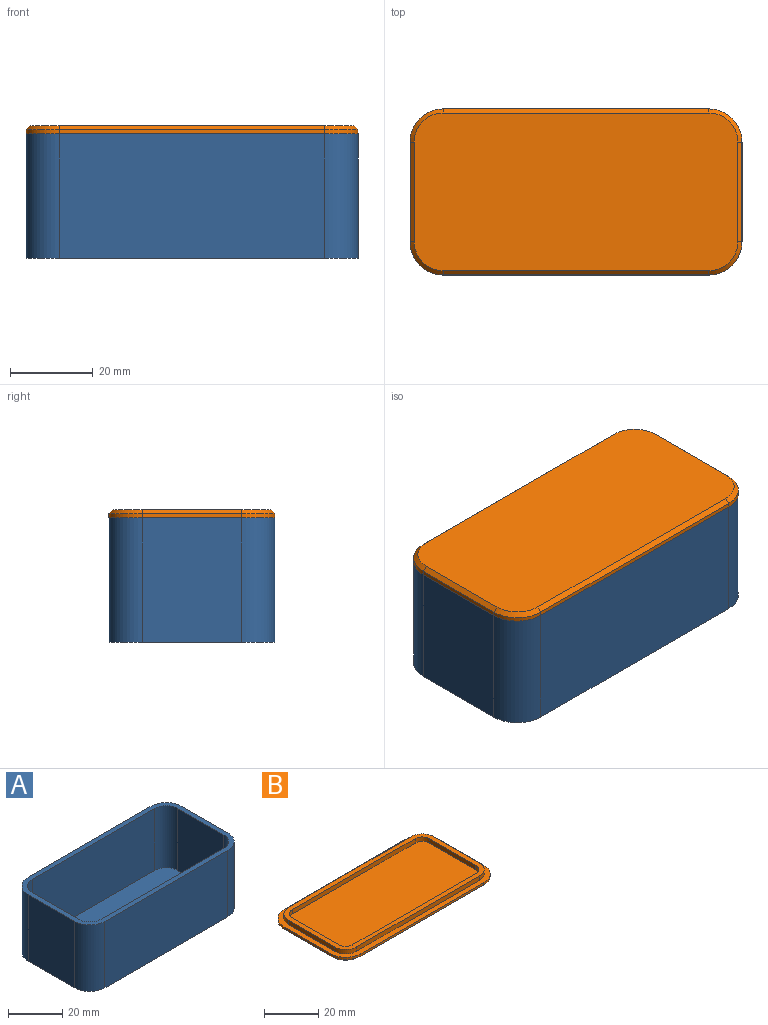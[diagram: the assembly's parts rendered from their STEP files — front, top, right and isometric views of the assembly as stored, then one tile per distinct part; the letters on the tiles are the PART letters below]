
ASSEMBLY  parts=2 mates=1
PART A: 19 faces, bbox 80x40x30 mm
  f0: plane 80x40mm, normal (0,0,1), area 440mm2, adj f1,f2,f3,f4,f5,f6,f7,f8
  f1: plane 30x24mm, normal (1,0,0), area 720mm2, adj f0,f2,f8,f9
  f2: cylinder r=8mm len=30mm, axis (0,0,-1), area 377mm2, adj f0,f1,f3,f9
  f3: plane 64x30mm, normal (0,1,0), area 1920mm2, adj f0,f2,f4,f9
  f4: cylinder r=8mm len=30mm, axis (0,0,-1), area 377mm2, adj f0,f3,f5,f9
  f5: plane 30x24mm, normal (-1,0,0), area 720mm2, adj f0,f4,f6,f9
  f6: cylinder r=8mm len=30mm, axis (0,0,-1), area 377mm2, adj f0,f5,f7,f9
  f7: plane 64x30mm, normal (0,-1,0), area 1920mm2, adj f0,f6,f8,f9
  f8: cylinder r=8mm len=30mm, axis (0,0,-1), area 377mm2, adj f0,f1,f7,f9
  f9: plane 80x40mm, normal (0,0,-1), area 3145.1mm2, adj f1,f2,f3,f4,f5,f6,f7,f8
  f10: plane 28x24mm, normal (-1,0,0), area 672mm2, adj f0,f11,f17,f18
  f11: cylinder r=6mm len=28mm, axis (0,0,-1), area 263.9mm2, adj f0,f10,f12,f18
  f12: plane 64x28mm, normal (0,-1,0), area 1792mm2, adj f0,f11,f13,f18
  f13: cylinder r=6mm len=28mm, axis (0,0,-1), area 263.9mm2, adj f0,f12,f14,f18
  f14: plane 28x24mm, normal (1,0,0), area 672mm2, adj f0,f13,f15,f18
  f15: cylinder r=6mm len=28mm, axis (0,0,-1), area 263.9mm2, adj f0,f14,f16,f18
  f16: plane 64x28mm, normal (0,1,0), area 1792mm2, adj f0,f15,f17,f18
  f17: cylinder r=6mm len=28mm, axis (0,0,-1), area 263.9mm2, adj f0,f10,f16,f18
  f18: plane 76x36mm, normal (0,0,1), area 2705.1mm2, adj f10,f11,f12,f13,f14,f15,f16,f17
PART B: 36 faces, bbox 80x40x4 mm
  f0: plane 24x1mm, normal (1,0,0), area 24mm2, adj f1,f7,f8,f33
  f1: cylinder r=8mm len=8mm, axis (0,0,-1), area 12.6mm2, adj f0,f2,f8,f35
  f2: plane 64x1mm, normal (0,1,0), area 64mm2, adj f1,f3,f8,f34
  f3: cylinder r=8mm len=8mm, axis (0,0,-1), area 12.6mm2, adj f2,f4,f8,f32
  f4: plane 24x1mm, normal (-1,0,0), area 24mm2, adj f3,f5,f8,f30
  f5: cylinder r=8mm len=8mm, axis (0,0,-1), area 12.6mm2, adj f4,f6,f8,f28
  f6: plane 64x1mm, normal (0,-1,0), area 64mm2, adj f5,f7,f8,f29
  f7: cylinder r=8mm len=8mm, axis (0,0,-1), area 12.6mm2, adj f0,f6,f8,f31
  f8: plane 80x40mm, normal (0,0,1), area 482.6mm2, adj f0,f1,f2,f3,f4,f5,f6,f7
  f9: plane 78x38mm, normal (0,0,-1), area 2921.9mm2, adj f28,f29,f30,f31,f32,f33,f34,f35
  f10: cylinder r=5.8mm len=5.8mm, axis (0,0,-1), area 18.2mm2, adj f8,f11,f25,f26
  f11: plane 64x2mm, normal (0,1,0), area 128mm2, adj f8,f10,f12,f26
  f12: cylinder r=5.8mm len=5.8mm, axis (0,0,-1), area 18.2mm2, adj f8,f11,f13,f26
  f13: plane 24x2mm, normal (-1,0,0), area 48mm2, adj f8,f12,f14,f26
  f14: cylinder r=5.8mm len=5.8mm, axis (0,0,-1), area 18.2mm2, adj f8,f13,f15,f26
  f15: plane 64x2mm, normal (0,-1,0), area 128mm2, adj f8,f14,f16,f26
  f16: cylinder r=5.8mm len=5.8mm, axis (0,0,-1), area 18.2mm2, adj f8,f15,f25,f26
  f17: cylinder r=3.8mm len=3.8mm, axis (0,0,-1), area 11.9mm2, adj f18,f24,f26,f27
  f18: plane 24x2mm, normal (-1,0,0), area 48mm2, adj f17,f19,f26,f27
  f19: cylinder r=3.8mm len=3.8mm, axis (0,0,-1), area 11.9mm2, adj f18,f20,f26,f27
  f20: plane 64x2mm, normal (0,1,0), area 128mm2, adj f19,f21,f26,f27
  f21: cylinder r=3.8mm len=3.8mm, axis (0,0,-1), area 11.9mm2, adj f20,f22,f26,f27
  f22: plane 24x2mm, normal (1,0,0), area 48mm2, adj f21,f23,f26,f27
  f23: cylinder r=3.8mm len=3.8mm, axis (0,0,-1), area 11.9mm2, adj f22,f24,f26,f27
  f24: plane 64x2mm, normal (0,-1,0), area 128mm2, adj f17,f23,f26,f27
  f25: plane 24x2mm, normal (1,0,0), area 48mm2, adj f8,f10,f16,f26
  f26: plane 75.6x35.6mm, normal (0,0,1), area 412.3mm2, adj f10,f11,f12,f13,f14,f15,f16,f17
  f27: plane 71.6x31.6mm, normal (0,0,1), area 2250.2mm2, adj f17,f18,f19,f20,f21,f22,f23,f24
  f28: cone r=8mm half-angle=45deg, axis (0,0,1), area 16.7mm2, adj f5,f9,f29,f30
  f29: plane 64x1mm, normal (0,-0.71,-0.71), area 90.5mm2, adj f6,f9,f28,f31
  f30: plane 24x1mm, normal (-0.71,0,-0.71), area 33.9mm2, adj f4,f9,f28,f32
  f31: cone r=8mm half-angle=45deg, axis (0,0,1), area 16.7mm2, adj f7,f9,f29,f33
  f32: cone r=8mm half-angle=45deg, axis (0,0,1), area 16.7mm2, adj f3,f9,f30,f34
  f33: plane 24x1mm, normal (0.71,0,-0.71), area 33.9mm2, adj f0,f9,f31,f35
  f34: plane 64x1mm, normal (0,0.71,-0.71), area 90.5mm2, adj f2,f9,f32,f35
  f35: cone r=8mm half-angle=45deg, axis (0,0,1), area 16.7mm2, adj f1,f9,f33,f34
PLACE A rot(axis=(0,0,1),180deg) t=(0,0,0)mm
PLACE B rot(axis=(1,0,0),180deg) t=(0,0,32)mm
MATE fastened A.f4 <-> B.f1  axis (0,0,1) through (32,-12,30)mm
